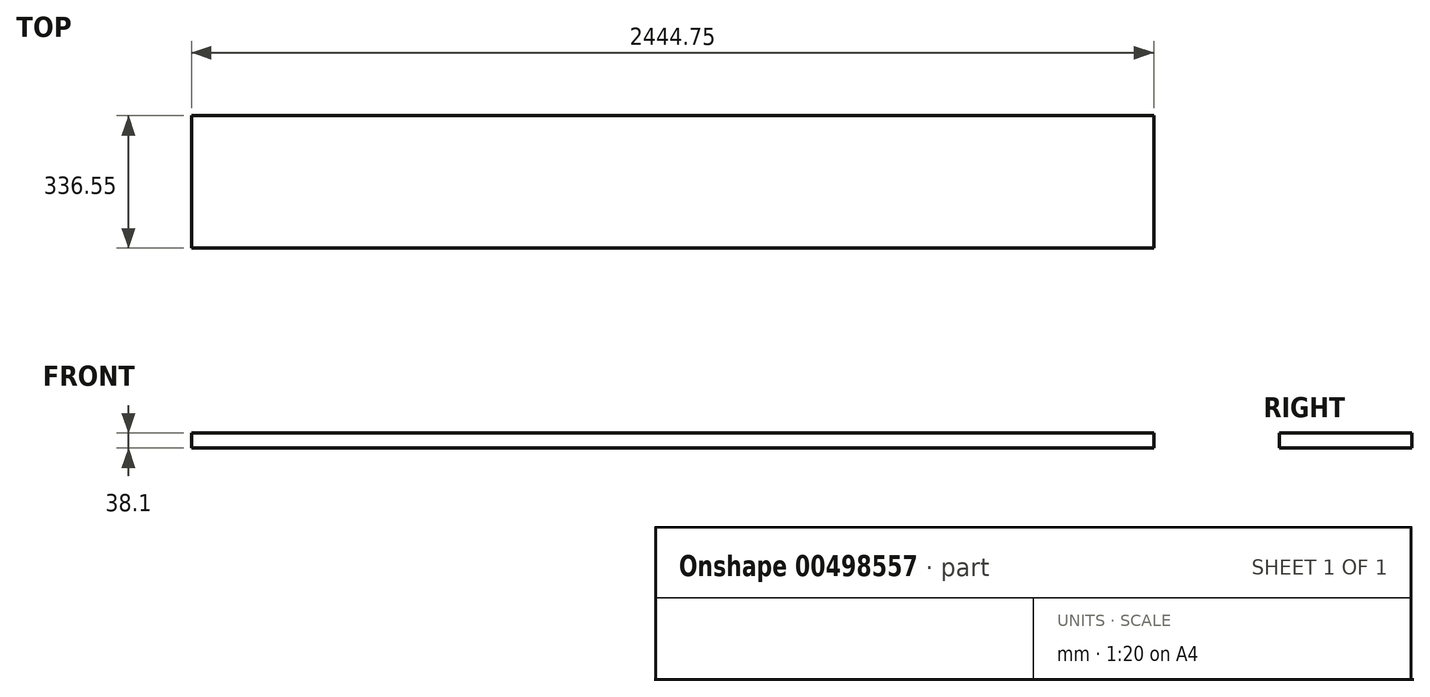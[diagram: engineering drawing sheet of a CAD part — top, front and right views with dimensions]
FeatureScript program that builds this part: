
annotation { "Feature Type Name" : "Feature", "Feature Type Description" : "" }
export const myFeature = defineFeature(function(context is Context, id is Id, definition is map)
    precondition{}
    {
        {
            var Q0;
            Q0=qCreatedBy(makeId("Top.planeOp"),FACE);
            var sketch = newSketch(context, id + "F0", { "sketchPlane" : qUnion([Q0])});
            skLineSegment(sketch, "E0.bottom", {"start": v(0, 0) * mm, "end": v(2444.75, 0) * mm});
            skLineSegment(sketch, "E0.top", {"start": v(0, 336.55) * mm, "end": v(2444.75, 336.55) * mm});
            skLineSegment(sketch, "E0.left", {"start": v(0, 0) * mm, "end": v(0, 336.55) * mm});
            skLineSegment(sketch, "E0.right", {"start": v(2444.75, 0) * mm, "end": v(2444.75, 336.55) * mm});
            skSolve(sketch);
        }
        {
            var Q0;
            Q0 = qSketchRegion(id + "F0", true);
            extrude(context, id + "F1", {"entities" : qUnion([Q0]), "depth" : 38.1 * mm});
        }
    });
